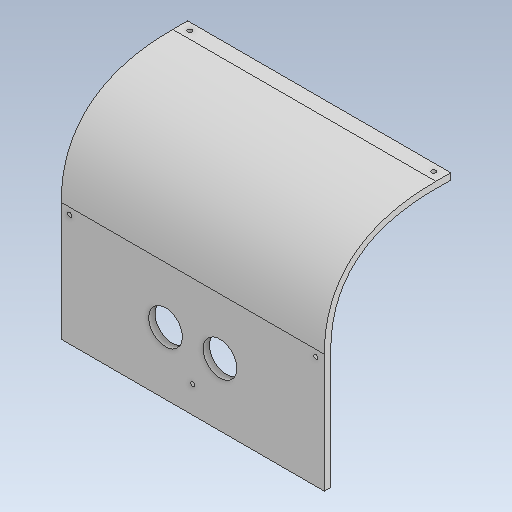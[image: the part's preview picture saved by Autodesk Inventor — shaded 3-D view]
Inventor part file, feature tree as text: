
AUTODESK INVENTOR PART (.ipt)
format: ipt  version: 2020 (Build 240168000, 168)  size: 157,696 bytes
history: native  units: mm
features: other x28, extrude x4, sketch x4
ambient origin geometry x8: Origin, YZ Plane, XZ Plane, XY Plane, X Axis, Y Axis, Z Axis, Center Point
bodies: Body1 (feature_tree)
feature tree (36):
  other  "Sólido1"
  extrude  "Extrusão1"  Depth=3.0mm TaperAngle=0.0deg
  extrude  "Extrusão2"  Depth=123.6mm TaperAngle=0.0deg
  extrude  "Extrusão3"  Depth=6.0mm TaperAngle=0.0deg
  extrude  "Extrusão4"  [1 undecoded]
  sketch  "Esboço1"  dims[d0=0.0mm d1=3.0mm d2=0.0mm]
  other  "Referência1"
  other  "Referência2"
  other  "Referência3"
  other  "Referência4"
  other  "Referência5"
  other  "Referência6"
  other  "Referência7"
  other  "Referência8"
  other  "Referência9"
  other  "Referência10"
  sketch  "Esboço2"  dims[d3=7.0mm d4=123.6mm d5=0.0mm]
  other  "Referência11"
  sketch  "Esboço3"  dims[d6=6.0mm d7=0.0mm d8=6.0mm d9=0.0mm]
  other  "Referência12"
  other  "Referência13"
  sketch  "Esboço4"
  other  "Referência14"
  other  "Referência15"
  other  "<userpath>\Desktop\rabo\3d\ela.iam"
  other  "ela.iam"
  other  "basesinha:1"
  other  "56145_Wheel:2"
  other  "Component2_32:2"
  other  "lateral_V2:1"
  other  "56145_Wheel_MIR:2"
  other  "ultrassonicohc-sr04:1"
  other  "apoio ultrassonico:1"
  other  "PCB:1"
  other  "canto:1"
  other  "canto_MIR1:1"
note: 1 required parameter value undecoded (feature->parameter linkage not recoverable at this tier; creation-order binding heuristic only, values carry confidence <= 0.55)
